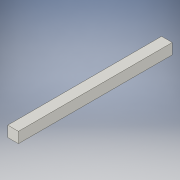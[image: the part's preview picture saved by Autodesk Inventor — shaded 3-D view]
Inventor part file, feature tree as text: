
AUTODESK INVENTOR PART (.ipt)
format: ipt  version: 2018 (Build 220112000, 112)  size: 91,648 bytes
history: native  units: in
note: dims shown in document units (in); Inventor stores cm internally (conversion verified against a paired STEP export)
features: extrude x1, sketch x1
ambient origin geometry x8: Origin, YZ Plane, XZ Plane, XY Plane, X Axis, Y Axis, Z Axis, Center Point
bodies: Solid1 (feature_tree)
feature tree (2):
  extrude  "Extrusion1"  Depth=0.1562in
  sketch  "Sketch1"  dims[d0=0.1562in d1=0.1562in d2=2.25in d3=0.0in]
